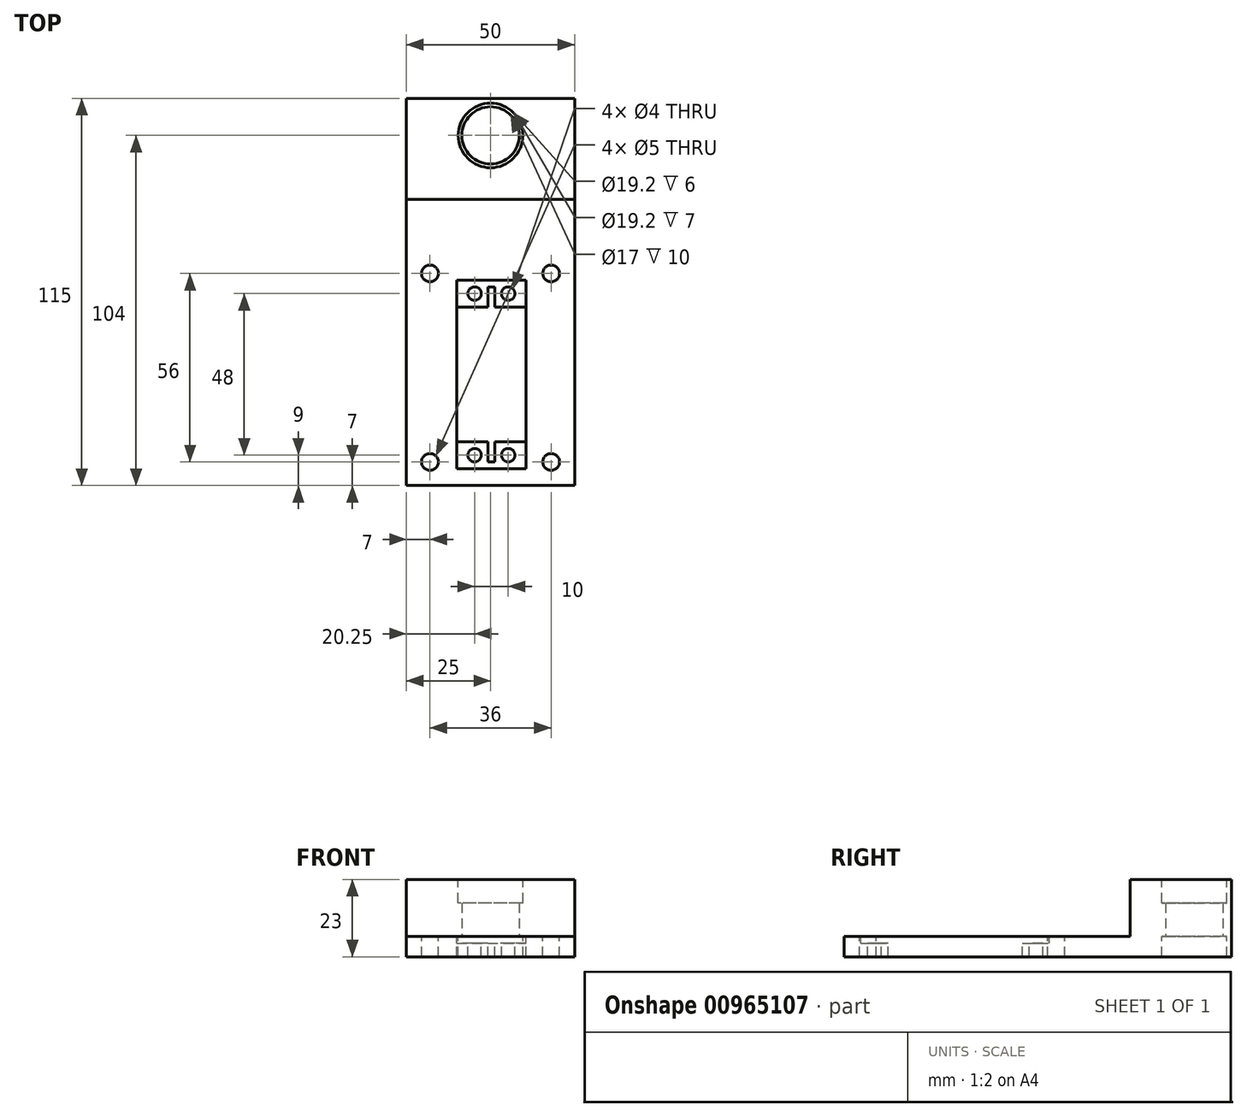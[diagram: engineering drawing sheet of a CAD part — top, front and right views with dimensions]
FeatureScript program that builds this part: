
annotation { "Feature Type Name" : "Feature", "Feature Type Description" : "" }
export const myFeature = defineFeature(function(context is Context, id is Id, definition is map)
    precondition{}
    {
        {
            var Q0;
            Q0=qCreatedBy(makeId("Top.planeOp"),FACE);
            var sketch = newSketch(context, id + "F0", { "sketchPlane" : qUnion([Q0])});
            skLineSegment(sketch, "E0.bottom", {"start": v(0, 0) * mm, "end": v(50, 0) * mm});
            skLineSegment(sketch, "E0.top", {"start": v(0, 115) * mm, "end": v(50, 115) * mm});
            skLineSegment(sketch, "E0.left", {"start": v(0, 0) * mm, "end": v(0, 115) * mm});
            skLineSegment(sketch, "E0.right", {"start": v(50, 0) * mm, "end": v(50, 115) * mm});
            skLineSegment(sketch, "E1.bottom", {"start": v(15, 5) * mm, "end": v(35.5, 5) * mm});
            skLineSegment(sketch, "E1.top", {"start": v(15, 61) * mm, "end": v(35.5, 61) * mm});
            skLineSegment(sketch, "E1.left", {"start": v(15, 5) * mm, "end": v(15, 61) * mm});
            skLineSegment(sketch, "E1.right", {"start": v(35.5, 5) * mm, "end": v(35.5, 61) * mm});
            skLineSegment(sketch, "E2", {"start": v(35.5, 53) * mm, "end": v(15, 53) * mm});
            skLineSegment(sketch, "E3", {"start": v(35.5, 13) * mm, "end": v(15, 13) * mm});
            skCircle(sketch, "E4", {"center": v(20.25, 57) * mm, "radius": 2 * mm});
            skCircle(sketch, "E5", {"center": v(30.25, 57) * mm, "radius": 2 * mm});
            skCircle(sketch, "E6", {"center": v(20.25, 9) * mm, "radius": 2 * mm});
            skCircle(sketch, "E7", {"center": v(30.25, 9) * mm, "radius": 2 * mm});
            skCircle(sketch, "E8", {"center": v(7, 63) * mm, "radius": 2.5 * mm});
            skCircle(sketch, "E9", {"center": v(43, 63) * mm, "radius": 2.5 * mm});
            skCircle(sketch, "E10", {"center": v(7, 7) * mm, "radius": 2.5 * mm});
            skCircle(sketch, "E11", {"center": v(43, 7) * mm, "radius": 2.5 * mm});
            skLineSegment(sketch, "E12.bottom", {"start": v(26.25, 53) * mm, "end": v(24.25, 53) * mm});
            skLineSegment(sketch, "E12.top", {"start": v(26.25, 59) * mm, "end": v(24.25, 59) * mm});
            skLineSegment(sketch, "E12.left", {"start": v(26.25, 53) * mm, "end": v(26.25, 59) * mm});
            skLineSegment(sketch, "E12.right", {"start": v(24.25, 53) * mm, "end": v(24.25, 59) * mm});
            skLineSegment(sketch, "E13.bottom", {"start": v(24.25, 13) * mm, "end": v(26.25, 13) * mm});
            skLineSegment(sketch, "E13.top", {"start": v(24.25, 7) * mm, "end": v(26.25, 7) * mm});
            skLineSegment(sketch, "E13.left", {"start": v(24.25, 13) * mm, "end": v(24.25, 7) * mm});
            skLineSegment(sketch, "E13.right", {"start": v(26.25, 13) * mm, "end": v(26.25, 7) * mm});
            skPoint(sketch, "E14", {"position": v(25, 44) * mm});
            skPoint(sketch, "E15", {"position": v(25, 104) * mm});
            skCircle(sketch, "E16", {"center": v(25, 104) * mm, "radius": 9.6 * mm});
            skLineSegment(sketch, "E17.top", {"start": v(0, 85) * mm, "end": v(50, 85) * mm});
            skLineSegment(sketch, "E17.left", {"start": v(0, 115) * mm, "end": v(0, 85) * mm});
            skLineSegment(sketch, "E17.right", {"start": v(50, 115) * mm, "end": v(50, 85) * mm});
            skCircle(sketch, "E18", {"center": v(25, 104) * mm, "radius": 8.5 * mm});
            skSolve(sketch);
        }
        {
            var Q0;
            Q0=makeQuery(id+"F0.imprint","IMPRINT",FACE,{"disambiguationData":[TD([[makeQuery(id+"F0.imprint","IMPRINT",EDGE,{"derivedFrom":sQuery(id+"F0.wireOp",EDGE,"E0.bottom")}),1.0]])]});
            var Q1;
            {var subQ2=sQuery(id+"F0.wireOp",EDGE,"E1.top");Q1=makeQuery(id+"F0.imprint","IMPRINT",FACE,{"disambiguationData":[TD([[makeQuery(id+"F0.imprint","IMPRINT",EDGE,{"derivedFrom":subQ2}),-1.0]])]});}
            var Q2;
            {var subQ2=sQuery(id+"F0.wireOp",EDGE,"E1.bottom");Q2=makeQuery(id+"F0.imprint","IMPRINT",FACE,{"disambiguationData":[TD([[makeQuery(id+"F0.imprint","IMPRINT",EDGE,{"derivedFrom":subQ2}),1.0]])]});}
            var Q3;
            Q3=makeQuery(id+"F0.imprint","IMPRINT",FACE,{"disambiguationData":[TD([[makeQuery(id+"F0.imprint","IMPRINT",EDGE,{"derivedFrom":sQuery(id+"F0.wireOp",EDGE,"E16")}),-1.0]])]});
            extrude(context, id + "F1", {"entities" : qUnion([Q0, Q1, Q2, Q3]), "oppositeDirection" : true, "depth" : 6 * mm, "offsetDistance" : 25 * mm});
        }
        {
            var Q0;
            {var subQ2=sQuery(id+"F0.wireOp",EDGE,"E1.top");Q0=makeQuery(id+"F0.imprint","IMPRINT",FACE,{"disambiguationData":[TD([[makeQuery(id+"F0.imprint","IMPRINT",EDGE,{"derivedFrom":subQ2}),-1.0]])]});}
            var Q1;
            {var subQ2=sQuery(id+"F0.wireOp",EDGE,"E1.bottom");Q1=makeQuery(id+"F0.imprint","IMPRINT",FACE,{"disambiguationData":[TD([[makeQuery(id+"F0.imprint","IMPRINT",EDGE,{"derivedFrom":subQ2}),1.0]])]});}
            extrude(context, id + "F2", {"entities" : qUnion([Q0, Q1]), "operationType" : NewBodyOperationType.REMOVE, "oppositeDirection" : true, "depth" : 2 * mm, "offsetDistance" : 25 * mm});
        }
        {
            var Q0;
            Q0=makeQuery(id+"F0.imprint","IMPRINT",FACE,{"disambiguationData":[TD([[makeQuery(id+"F0.imprint","IMPRINT",EDGE,{"derivedFrom":sQuery(id+"F0.wireOp",EDGE,"E16")}),-1.0]])]});
            extrude(context, id + "F3", {"entities" : qUnion([Q0]), "operationType" : NewBodyOperationType.ADD, "depth" : 17 * mm, "offsetDistance" : 25 * mm});
        }
        {
            var Q0;
            Q0=makeQuery(id+"F0.imprint","IMPRINT",FACE,{"disambiguationData":[TD([[makeQuery(id+"F0.imprint","IMPRINT",EDGE,{"derivedFrom":sQuery(id+"F0.wireOp",EDGE,"E16")}),1.0]])]});
            extrude(context, id + "F4", {"entities" : qUnion([Q0]), "operationType" : NewBodyOperationType.ADD, "depth" : 10 * mm, "offsetDistance" : 25 * mm});
        }
    });
